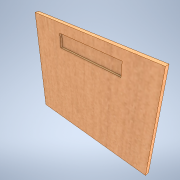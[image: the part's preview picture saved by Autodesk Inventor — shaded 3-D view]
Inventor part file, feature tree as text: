
AUTODESK INVENTOR PART (.ipt)
format: ipt  version: 2021 (Build 250183000, 183)  size: 134,656 bytes
history: native  units: mm
features: sketch x2, extrude x1
ambient origin geometry x8: Origin, YZ Plane, XZ Plane, XY Plane, X Axis, Y Axis, Z Axis, Center Point
bodies: Solid1 (feature_tree)
feature tree (3):
  extrude  "Extrusion1"  Depth=3.0mm TaperAngle=0.0deg
  sketch  "Sketch1"  dims[d1=77.0mm d2=3.0mm d3=0.0mm]
  sketch  "Sketch4"  dims[d47=50.0mm d48=10.0mm d49=1.5mm d50=0.0mm d51=99.0mm]
